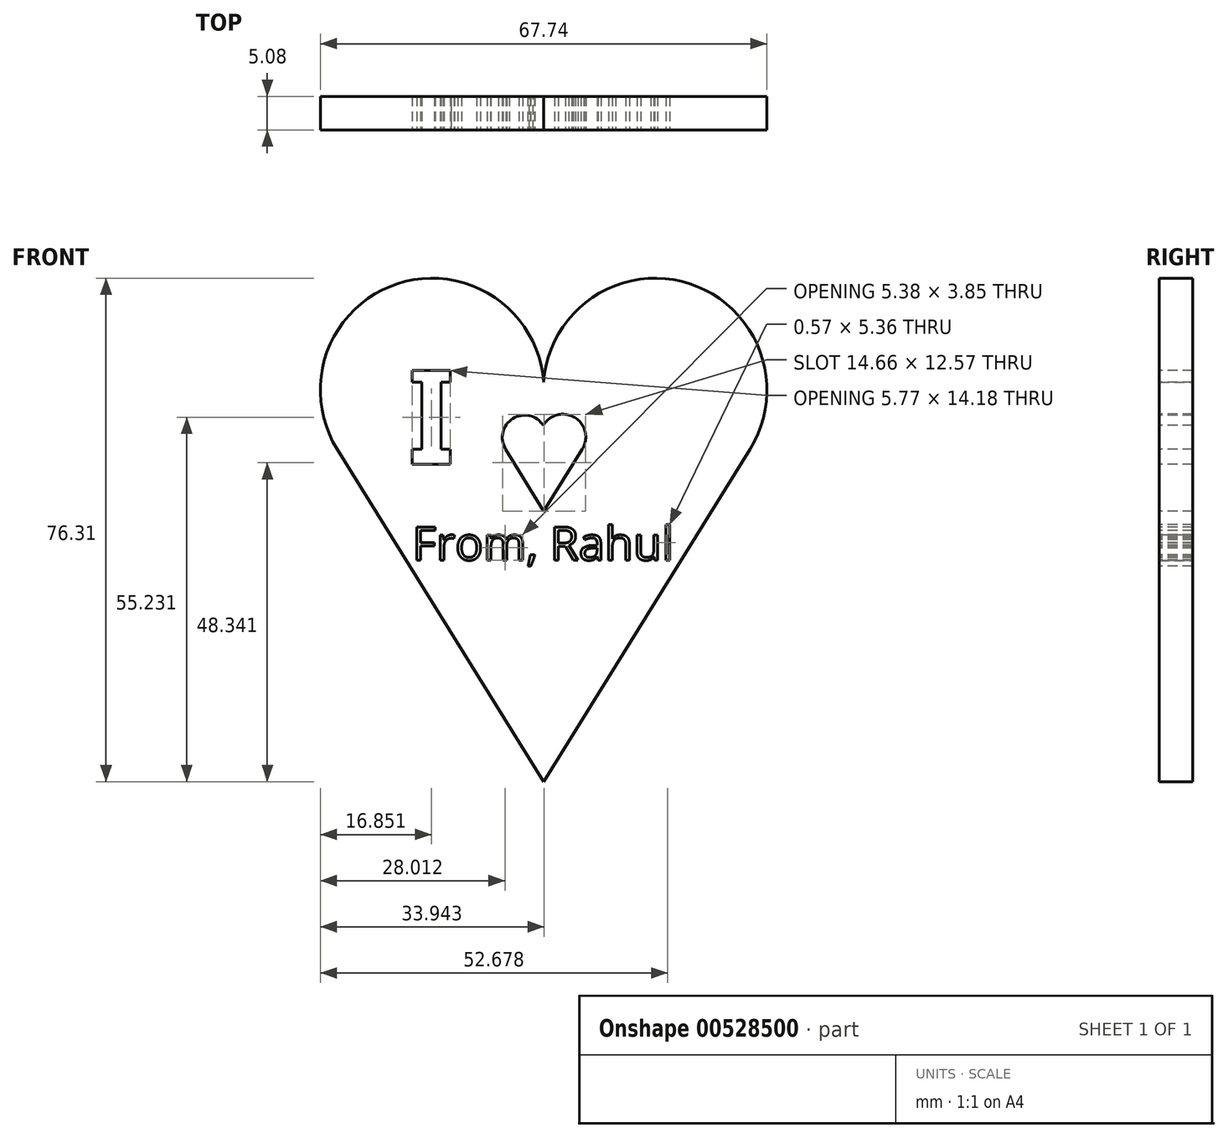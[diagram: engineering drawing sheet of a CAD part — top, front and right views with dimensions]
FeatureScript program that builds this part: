
annotation { "Feature Type Name" : "Feature", "Feature Type Description" : "" }
export const myFeature = defineFeature(function(context is Context, id is Id, definition is map)
    precondition{}
    {
        {
            var Q0;
            Q0=qCreatedBy(makeId("Front.planeOp"),FACE);
            var sketch = newSketch(context, id + "F0", { "sketchPlane" : qUnion([Q0])});
            skLineSegment(sketch, "E0", {"start": v(0, 75.88) * mm, "end": v(0, -76.22) * mm});
            skLineSegment(sketch, "E1", {"start": v(-31.32, 0) * mm, "end": v(0, -50.41) * mm});
            skLineSegment(sketch, "E2.MirrorCS", {"start": v(31.32, 0) * mm, "end": v(0, -50.41) * mm});
            skArc(sketch, "E3", {"start": v(0, 7.74) * mm, "mid": v(-20.98, 25.4) * mm, "end": v(-31.32, 0) * mm});
            skArc(sketch, "E4.MirrorCS", {"start": v(0, 7.74) * mm, "mid": v(20.98, 25.4) * mm, "end": v(31.32, 0) * mm});
            skSolve(sketch);
        }
        {
            var Q0;
            Q0 = qSketchRegion(id + "F0", true);
            extrude(context, id + "F1", {"entities" : qUnion([Q0]), "depth" : 5.08 * mm, "offsetDistance" : 25.4 * mm});
        }
        {
            var Q0;
            Q0=makeQuery(id+"F1.opExtrude","CAP_FACE",FACE,{"disambiguationData":[OSD([sQuery(id+"F0.wireOp",EDGE,"E1"),sQuery(id+"F0.wireOp",EDGE,"E2.MirrorCS"),sQuery(id+"F0.wireOp",EDGE,"E3"),sQuery(id+"F0.wireOp",EDGE,"E4.MirrorCS")])],"isStart":false});
            var sketch = newSketch(context, id + "F2", { "sketchPlane" : qUnion([Q0])});
            skLineSegment(sketch, "E5", {"start": v(-17.02, 11.91) * mm, "end": v(-19.9, 11.91) * mm});
            skLineSegment(sketch, "E6", {"start": v(-19.9, 11.91) * mm, "end": v(-19.9, 10.13) * mm});
            skLineSegment(sketch, "E7", {"start": v(-19.9, 10.13) * mm, "end": v(-18.46, 10.13) * mm});
            skPoint(sketch, "E7.endSnap0", {"position": v(-18.46, 11.91) * mm});
            skLineSegment(sketch, "E8", {"start": v(-18.46, 10.13) * mm, "end": v(-18.46, 0) * mm});
            skLineSegment(sketch, "E9", {"start": v(-18.46, 0) * mm, "end": v(-19.9, 0) * mm});
            skLineSegment(sketch, "E10", {"start": v(-19.9, 0) * mm, "end": v(-19.9, -2.27) * mm});
            skLineSegment(sketch, "E11", {"start": v(-19.9, -2.27) * mm, "end": v(-17.02, -2.27) * mm});
            skLineSegment(sketch, "E12.MirrorCS", {"start": v(-15.58, 10.13) * mm, "end": v(-15.58, 0) * mm});
            skLineSegment(sketch, "E13.MirrorCS", {"start": v(-14.13, 0) * mm, "end": v(-14.13, -2.27) * mm});
            skLineSegment(sketch, "E14.MirrorCS", {"start": v(-15.58, 0) * mm, "end": v(-14.13, 0) * mm});
            skLineSegment(sketch, "E15.MirrorCS", {"start": v(-14.13, -2.27) * mm, "end": v(-17.02, -2.27) * mm});
            skLineSegment(sketch, "E16.MirrorCS", {"start": v(-17.02, 11.91) * mm, "end": v(-14.13, 11.91) * mm});
            skLineSegment(sketch, "E17.MirrorCS", {"start": v(-14.13, 11.91) * mm, "end": v(-14.13, 10.13) * mm});
            skLineSegment(sketch, "E18.MirrorCS", {"start": v(-14.13, 10.13) * mm, "end": v(-15.58, 10.13) * mm});
            skLineSegment(sketch, "E19", {"start": v(-5.76, 0) * mm, "end": v(0, -9.4) * mm});
            skLineSegment(sketch, "E20", {"start": v(0, -9.4) * mm, "end": v(5.88, 0) * mm});
            skArc(sketch, "E21", {"start": v(-0.05, 3.6) * mm, "mid": v(-4.68, 4.62) * mm, "end": v(-5.76, 0) * mm});
            skArc(sketch, "E22", {"start": v(5.88, 0) * mm, "mid": v(4.74, 4.8) * mm, "end": v(-0.05, 3.6) * mm});
            skEllipticalArc(sketch, "E23", {});
            skLineSegment(sketch, "E24", {"start": v(12.94, 11.91) * mm, "end": v(14.86, 11.91) * mm});
            skLineSegment(sketch, "E25", {"start": v(20.34, 11.91) * mm, "end": v(22.26, 11.91) * mm});
            skPoint(sketch, "E26.end.orphan", {"position": v(-17.02, -3.83) * mm});
            const initialGuessF2  = {"E23": [0.01759989932179451, 0.011912536807358265, 0, -1, 0.013588287401944399, 0.004662767976046384, 4.71238898038469, 1.5707963267948966], "E23": [0.01759989932179451, 0.011912536807358265, 0, -1, 0.010982768377289176, 0.0027428157563876704, 4.71238898038469, 1.5707963267948966]};
            skSetInitialGuess(sketch, initialGuessF2);
            skSolve(sketch);
        }
        {
            var Q0;
            Q0 = qSketchRegion(id + "F2", true);
            extrude(context, id + "F3", {"entities" : qUnion([Q0]), "operationType" : NewBodyOperationType.REMOVE, "oppositeDirection" : true, "depth" : 25.4 * mm, "offsetDistance" : 25.4 * mm});
        }
        {
            var Q0;
            Q0=makeQuery(id+"F1.opExtrude","CAP_FACE",FACE,{"disambiguationData":[OSD([sQuery(id+"F0.wireOp",EDGE,"E1"),sQuery(id+"F0.wireOp",EDGE,"E2.MirrorCS"),sQuery(id+"F0.wireOp",EDGE,"E3"),sQuery(id+"F0.wireOp",EDGE,"E4.MirrorCS")])],"isStart":false});
            var sketch = newSketch(context, id + "F4", { "sketchPlane" : qUnion([Q0])});
            skText(sketch, "E27", { "text": "From, Rahul", "fontName": "OpenSans-Regular.ttf"});
            const initialGuessF4  = {"E27": [-0.01994, -0.01683, 1, 0, 0.00508]};
            skSetInitialGuess(sketch, initialGuessF4);
            skSolve(sketch);
        }
        {
            var Q0;
            Q0 = qSketchRegion(id + "F4", true);
            extrude(context, id + "F5", {"entities" : qUnion([Q0]), "operationType" : NewBodyOperationType.REMOVE, "oppositeDirection" : true, "depth" : 25.4 * mm, "offsetDistance" : 25.4 * mm});
        }
    });
